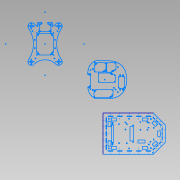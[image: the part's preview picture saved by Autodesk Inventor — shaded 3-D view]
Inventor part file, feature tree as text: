
AUTODESK INVENTOR PART (.ipt)
format: ipt  version: 2015 SP1 (Build 190203100, 203)  size: 237,056 bytes
history: native  units: mm
features: sketch x1
ambient origin geometry x8: Origin, YZ Plane, XZ Plane, XY Plane, X Axis, Y Axis, Z Axis, Center Point
feature tree (1):
  sketch  "Sketch1"  dims[d104=30.0mm d106=23.0mm d107=30.0mm d109=23.0mm d113=30.0mm d115=32.5mm d116=30.0mm d118=32.5mm d121=172.234468mm d123=172.234468mm d124=58.326098mm d125=58.326098mm d126=58.326098mm d127=23.561995mm d128=23.561874mm d129=23.562018mm d130=23.561892mm d131=15.707985mm d132=15.707942mm d133=10.0mm d134=10.0mm d135=9.999879mm d136=10.0mm d137=10.0mm d138=10.0mm d143=140.811657mm]
